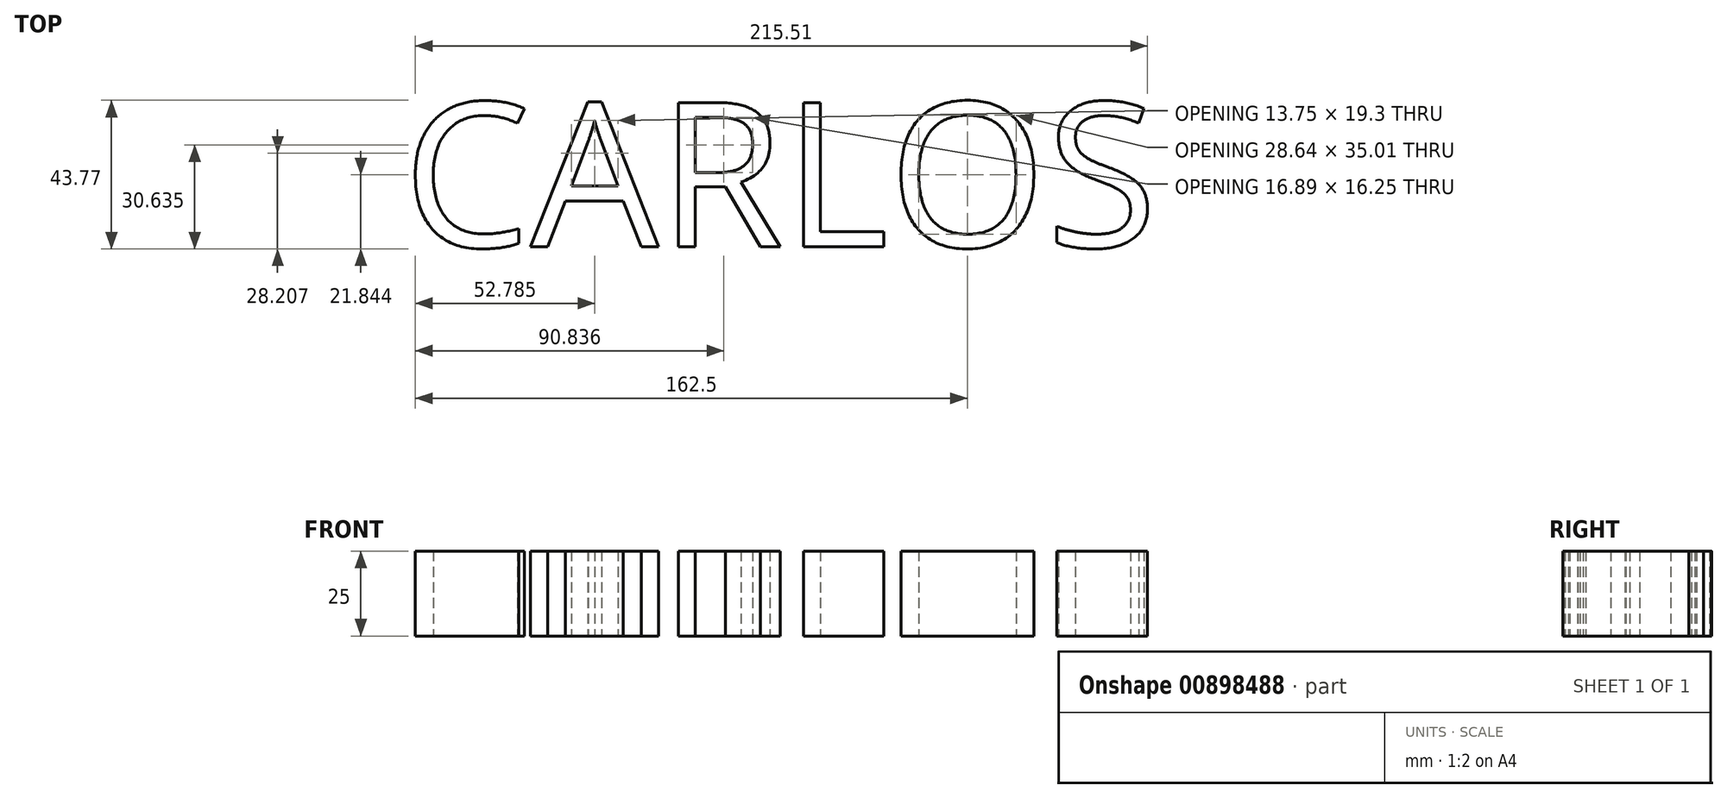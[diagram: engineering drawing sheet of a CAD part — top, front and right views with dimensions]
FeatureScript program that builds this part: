
annotation { "Feature Type Name" : "Feature", "Feature Type Description" : "" }
export const myFeature = defineFeature(function(context is Context, id is Id, definition is map)
    precondition{}
    {
        {
            var Q0;
            Q0=qCreatedBy(makeId("Top.planeOp"),FACE);
            var sketch = newSketch(context, id + "F0", { "sketchPlane" : qUnion([Q0])});
            skText(sketch, "E0", { "text": "CARLOS", "fontName": "OpenSans-Regular.ttf"});
            const initialGuessF0  = {"E0": [-0.05732, 0.00404, 1, 0, 0.04287]};
            skSetInitialGuess(sketch, initialGuessF0);
            skSolve(sketch);
        }
        {
            var Q0;
            Q0 = qSketchRegion(id + "F0", true);
            extrude(context, id + "F1", {"entities" : qUnion([Q0]), "depth" : 25 * mm, "offsetDistance" : 25 * mm});
        }
    });
